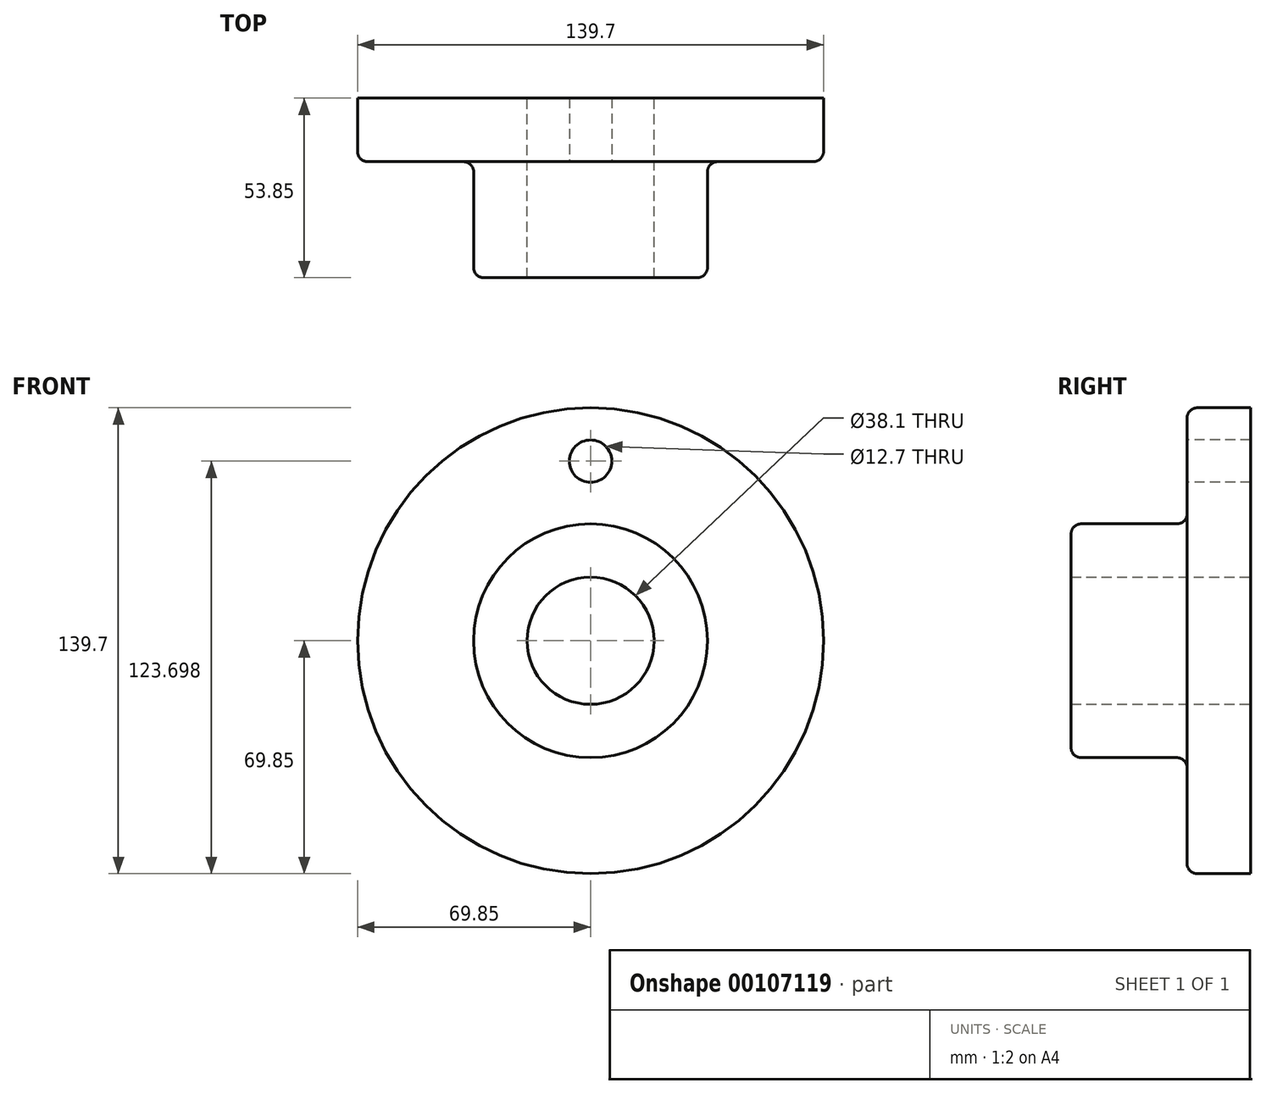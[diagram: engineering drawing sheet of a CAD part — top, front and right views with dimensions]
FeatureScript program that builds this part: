
annotation { "Feature Type Name" : "Feature", "Feature Type Description" : "" }
export const myFeature = defineFeature(function(context is Context, id is Id, definition is map)
    precondition{}
    {
        {
            var Q0;
            Q0=qCreatedBy(makeId("Right.planeOp"),FACE);
            var sketch = newSketch(context, id + "F0", { "sketchPlane" : qUnion([Q0])});
            skLineSegment(sketch, "E0", {"start": v(0, 0) * mm, "end": v(-63.18, 0) * mm, "construction": true});
            skLineSegment(sketch, "E1", {"start": v(0, 0) * mm, "end": v(0, 19.05) * mm, "construction": true});
            skLineSegment(sketch, "E2", {"start": v(0, 19.05) * mm, "end": v(0, 69.85) * mm});
            skLineSegment(sketch, "E3", {"start": v(0, 69.85) * mm, "end": v(-19.05, 69.85) * mm});
            skLineSegment(sketch, "E4", {"start": v(-19.05, 69.85) * mm, "end": v(-19.05, 35.05) * mm});
            skLineSegment(sketch, "E5", {"start": v(-19.05, 35.05) * mm, "end": v(-53.85, 35.05) * mm});
            skLineSegment(sketch, "E6", {"start": v(-53.85, 35.05) * mm, "end": v(-53.85, 19.05) * mm});
            skLineSegment(sketch, "E7", {"start": v(-53.85, 19.05) * mm, "end": v(0, 19.05) * mm});
            skSolve(sketch);
        }
        {
            var Q0;
            Q0=makeQuery(id+"F0.imprint","IMPRINT",FACE,{"disambiguationData":[TD([[makeQuery(id+"F0.imprint","IMPRINT",EDGE,{"derivedFrom":sQuery(id+"F0.wireOp",EDGE,"E2")}),1.0]])]});
            var Q1;
            Q1=sQuery(id+"F0.wireOp",EDGE,"E0");
            revolve(context, id + "F1", {"entities" : qUnion([Q0]), "axis" : qUnion([Q1]), "revolveType" : RevolveType.FULL});
        }
        {
            var Q0;
            Q0=makeQuery(id+"F1.opRevolve","SWEPT_EDGE",EDGE,{"disambiguationData":[OSD([sQuery(id+"F0.wireOp",EDGE,"E5"),sQuery(id+"F0.wireOp",EDGE,"E6")])]});
            var Q1;
            Q1=makeQuery(id+"F1.opRevolve","SWEPT_EDGE",EDGE,{"disambiguationData":[OSD([sQuery(id+"F0.wireOp",EDGE,"E4"),sQuery(id+"F0.wireOp",EDGE,"E5")])]});
            var Q2;
            Q2=makeQuery(id+"F1.opRevolve","SWEPT_EDGE",EDGE,{"disambiguationData":[OSD([sQuery(id+"F0.wireOp",EDGE,"E3"),sQuery(id+"F0.wireOp",EDGE,"E4")])]});
            fillet(context, id + "F2", {"entities" : qUnion([Q0, Q1, Q2]), "radius" : 3.05 * mm, "tangentPropagation" : true, "allowEdgeOverflow" : false});
        }
        {
            var Q0;
            Q0=makeQuery(id+"F1.opRevolve","SWEPT_FACE",FACE,{"disambiguationData":[OSD([sQuery(id+"F0.wireOp",EDGE,"E4")])]});
            var sketch = newSketch(context, id + "F3", { "sketchPlane" : qUnion([Q0])});
            skCircle(sketch, "E8", {"center": v(0, 0) * mm, "radius": 53.85 * mm, "construction": true});
            skCircle(sketch, "E9", {"center": v(0, 53.85) * mm, "radius": 6.35 * mm});
            skSolve(sketch);
        }
        {
            var Q0;
            Q0 = qSketchRegion(id + "F3", true);
            extrude(context, id + "F4", {"entities" : qUnion([Q0]), "operationType" : NewBodyOperationType.REMOVE, "endBound" : BoundingType.THROUGH_ALL, "oppositeDirection" : true, "depth" : 25.4 * mm});
        }
    });
